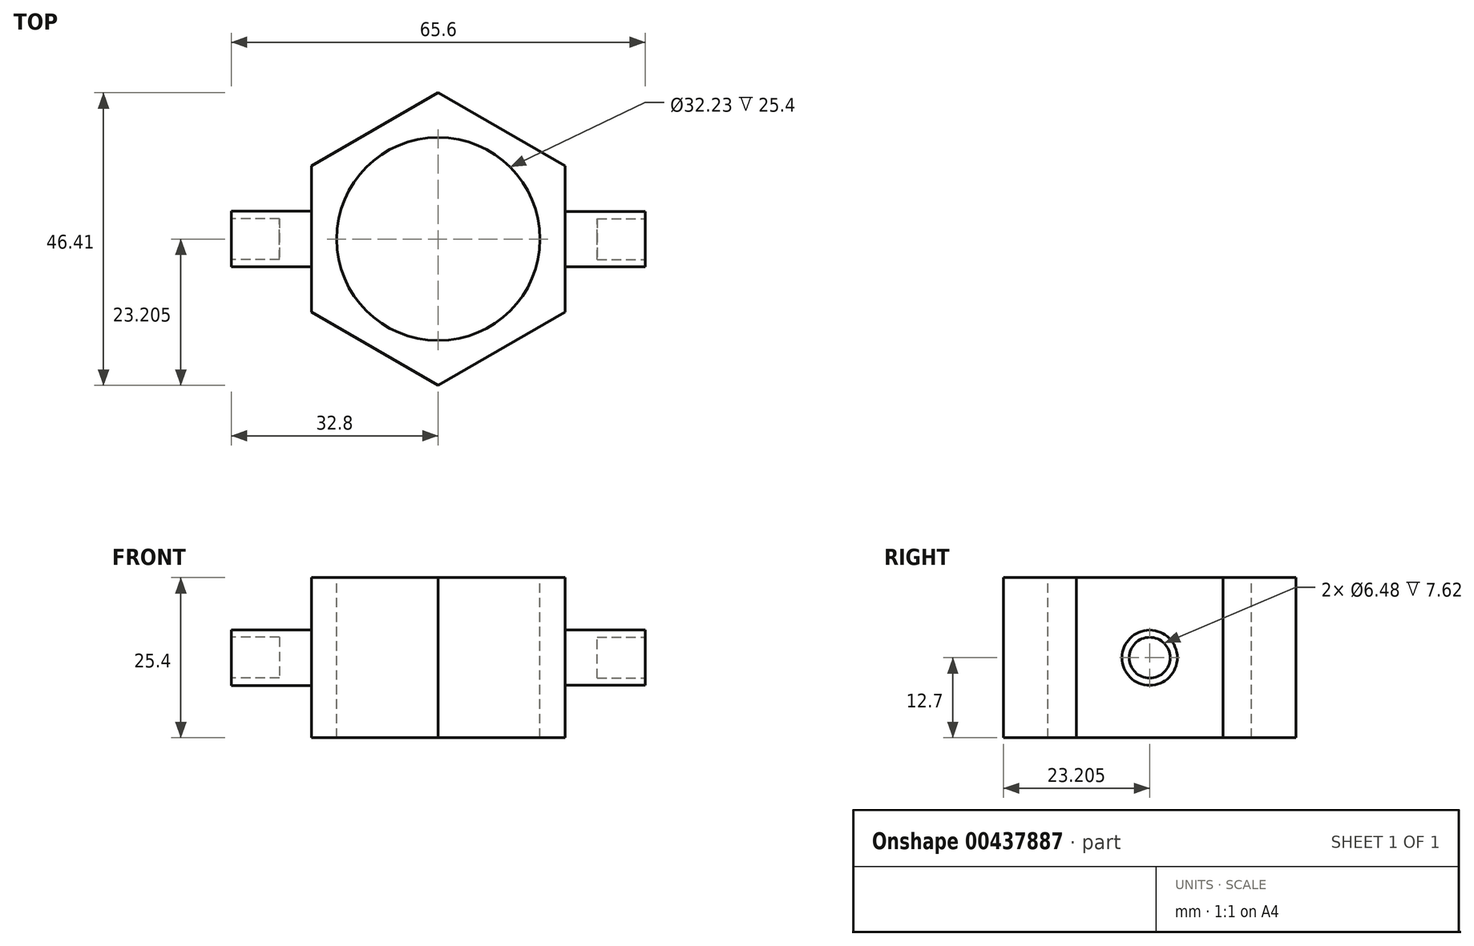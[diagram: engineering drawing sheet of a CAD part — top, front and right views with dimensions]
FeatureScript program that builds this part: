
annotation { "Feature Type Name" : "Feature", "Feature Type Description" : "" }
export const myFeature = defineFeature(function(context is Context, id is Id, definition is map)
    precondition{}
    {
        {
            var Q0;
            Q0=qCreatedBy(makeId("Top.planeOp"),FACE);
            var sketch = newSketch(context, id + "F0", { "sketchPlane" : qUnion([Q0])});
            skCircle(sketch, "E0.cCircle", {"center": v(0, -14) * mm, "radius": 20.1 * mm, "construction": true});
            skLineSegment(sketch, "E0.0", {"start": v(-20.1, -25.6) * mm, "end": v(-20.1, -2.4) * mm});
            skLineSegment(sketch, "E0.1", {"start": v(-20.1, -2.4) * mm, "end": v(0, 9.2) * mm});
            skLineSegment(sketch, "E0.2", {"start": v(0, 9.2) * mm, "end": v(20.1, -2.4) * mm});
            skLineSegment(sketch, "E0.3", {"start": v(20.1, -2.4) * mm, "end": v(20.1, -25.6) * mm});
            skLineSegment(sketch, "E0.4", {"start": v(20.1, -25.6) * mm, "end": v(0, -37.21) * mm});
            skLineSegment(sketch, "E0.5", {"start": v(0, -37.21) * mm, "end": v(-20.1, -25.6) * mm});
            skPoint(sketch, "E0.0.midPoint", {"position": v(-20.1, -14) * mm});
            skSolve(sketch);
        }
        {
            var Q0;
            Q0=qSketchRegion(id+"F0",true);
            extrude(context, id + "F1", {"entities" : qUnion([Q0]), "depth" : 25.4 * mm, "symmetric" : true});
        }
        {
            var Q0;
            Q0=makeQuery(id+"F1.opExtrude","CAP_FACE",FACE,{"disambiguationData":[OSD([sQuery(id+"F0.wireOp",EDGE,"E0.0"),sQuery(id+"F0.wireOp",EDGE,"E0.1"),sQuery(id+"F0.wireOp",EDGE,"E0.2"),sQuery(id+"F0.wireOp",EDGE,"E0.3"),sQuery(id+"F0.wireOp",EDGE,"E0.4"),sQuery(id+"F0.wireOp",EDGE,"E0.5")])],"isStart":false});
            var sketch = newSketch(context, id + "F2", { "sketchPlane" : qUnion([Q0])});
            skCircle(sketch, "E1", {"center": v(0, -14) * mm, "radius": 16.12 * mm});
            skPoint(sketch, "E1.centerSnap0", {"position": v(-20.1, -14) * mm});
            skSolve(sketch);
        }
        {
            var Q0;
            Q0=qSketchRegion(id+"F2",true);
            extrude(context, id + "F3", {"entities" : qUnion([Q0]), "operationType" : NewBodyOperationType.REMOVE, "oppositeDirection" : true, "depth" : 25.4 * mm});
        }
        {
            var Q0;
            Q0=makeQuery(id+"F1.opExtrude","SWEPT_FACE",FACE,{"disambiguationData":[OSD([sQuery(id+"F0.wireOp",EDGE,"E0.0")])]});
            var sketch = newSketch(context, id + "F4", { "sketchPlane" : qUnion([Q0])});
            skCircle(sketch, "E2", {"center": v(14, 0) * mm, "radius": 4.43 * mm});
            skPoint(sketch, "E2.centerSnap0", {"position": v(14, 12.7) * mm});
            skPoint(sketch, "E2.centerSnap1", {"position": v(2.4, 0) * mm});
            skSolve(sketch);
        }
        {
            var Q0;
            Q0=makeQuery(id+"F4.imprint","IMPRINT",FACE,{"disambiguationData":[TD([[makeQuery(id+"F4.imprint","IMPRINT",EDGE,{"derivedFrom":sQuery(id+"F4.wireOp",EDGE,"E2")}),1.0]])]});
            extrude(context, id + "F5", {"entities" : qUnion([Q0]), "operationType" : NewBodyOperationType.ADD, "depth" : 12.7 * mm});
        }
        {
            var Q0;
            Q0=makeQuery(id+"F1.opExtrude","SWEPT_FACE",FACE,{"disambiguationData":[OSD([sQuery(id+"F0.wireOp",EDGE,"E0.3")])]});
            var sketch = newSketch(context, id + "F6", { "sketchPlane" : qUnion([Q0])});
            skCircle(sketch, "E3", {"center": v(-14, 0) * mm, "radius": 4.38 * mm});
            skPoint(sketch, "E3.centerSnap0", {"position": v(-2.4, 0) * mm});
            skPoint(sketch, "E3.centerSnap1", {"position": v(-14, 12.7) * mm});
            skSolve(sketch);
        }
        {
            var Q0;
            Q0=qSketchRegion(id+"F6",true);
            extrude(context, id + "F7", {"entities" : qUnion([Q0]), "operationType" : NewBodyOperationType.ADD, "depth" : 12.7 * mm});
        }
        {
            var Q0;
            Q0=makeQuery(id+"F5.opExtrude","CAP_FACE",FACE,{"disambiguationData":[OSD([sQuery(id+"F4.wireOp",EDGE,"E2")])],"isStart":false});
            var sketch = newSketch(context, id + "F8", { "sketchPlane" : qUnion([Q0])});
            skCircle(sketch, "E4", {"center": v(14, 0) * mm, "radius": 3.24 * mm});
            skSolve(sketch);
        }
        {
            var Q0;
            Q0 = qSketchRegion(id + "F8", true);
            extrude(context, id + "F9", {"entities" : qUnion([Q0]), "operationType" : NewBodyOperationType.REMOVE, "oppositeDirection" : true, "depth" : 7.62 * mm});
        }
        {
            var Q0;
            Q0=makeQuery(id+"F7.opExtrude","CAP_FACE",FACE,{"disambiguationData":[OSD([sQuery(id+"F6.wireOp",EDGE,"E3")])],"isStart":false});
            var sketch = newSketch(context, id + "F10", { "sketchPlane" : qUnion([Q0])});
            skCircle(sketch, "E5", {"center": v(-14, 0) * mm, "radius": 3.24 * mm});
            skSolve(sketch);
        }
        {
            var Q0;
            Q0 = qSketchRegion(id + "F10", true);
            extrude(context, id + "F11", {"entities" : qUnion([Q0]), "operationType" : NewBodyOperationType.REMOVE, "oppositeDirection" : true, "depth" : 7.62 * mm});
        }
    });
